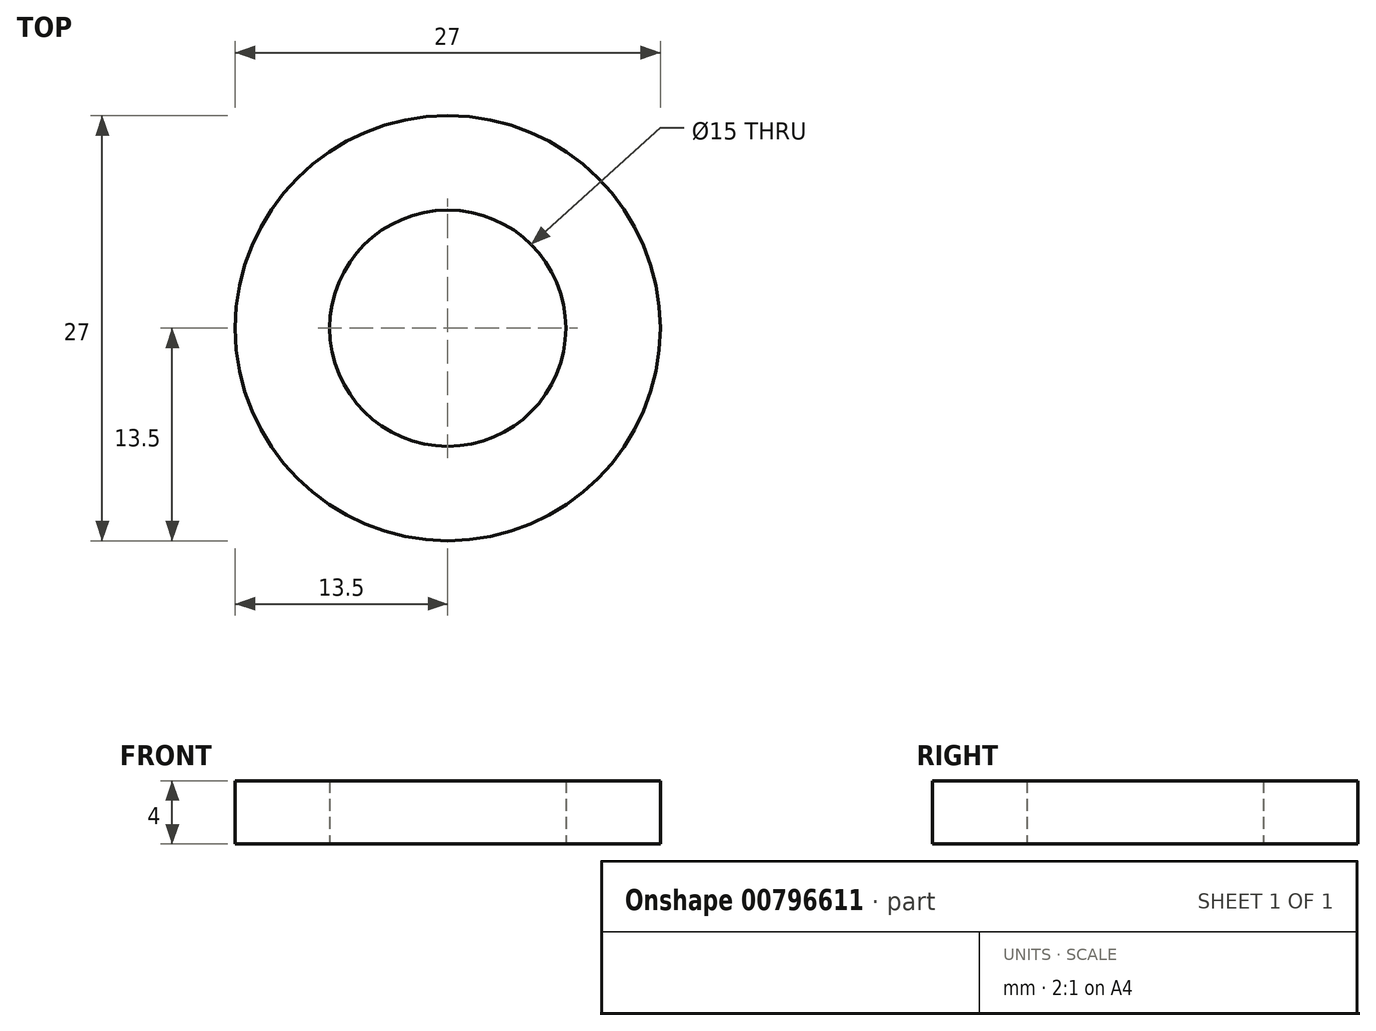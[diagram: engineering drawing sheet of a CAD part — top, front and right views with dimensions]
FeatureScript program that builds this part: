
annotation { "Feature Type Name" : "Feature", "Feature Type Description" : "" }
export const myFeature = defineFeature(function(context is Context, id is Id, definition is map)
    precondition{}
    {
        {
            var Q0;
            Q0=qCreatedBy(makeId("Top.planeOp"),FACE);
            var sketch = newSketch(context, id + "F0", { "sketchPlane" : qUnion([Q0])});
            skCircle(sketch, "E0", {"center": v(0, 0) * mm, "radius": 13.5 * mm});
            skCircle(sketch, "E1", {"center": v(0, 0) * mm, "radius": 7.5 * mm});
            skSolve(sketch);
        }
        {
            var Q0;
            Q0=makeQuery(id+"F0.imprint","IMPRINT",FACE,{"disambiguationData":[TD([[makeQuery(id+"F0.imprint","IMPRINT",EDGE,{"derivedFrom":sQuery(id+"F0.wireOp",EDGE,"E0")}),1.0]])]});
            extrude(context, id + "F1", {"entities" : qUnion([Q0]), "depth" : 4 * mm, "offsetDistance" : 25.4 * mm});
        }
    });
